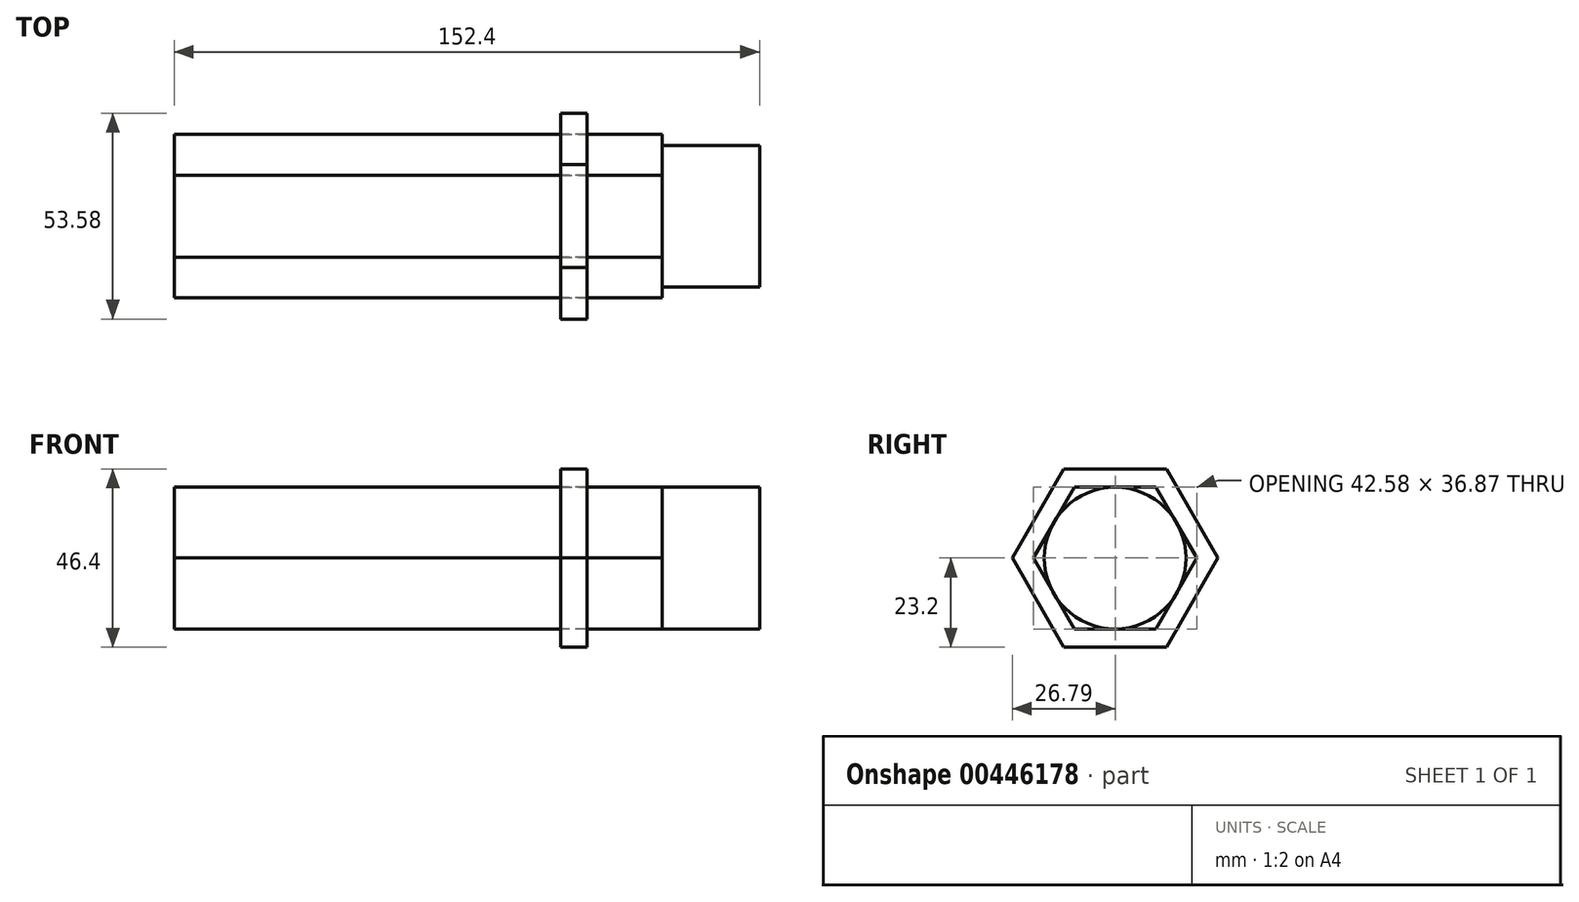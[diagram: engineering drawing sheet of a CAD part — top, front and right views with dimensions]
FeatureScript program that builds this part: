
annotation { "Feature Type Name" : "Feature", "Feature Type Description" : "" }
export const myFeature = defineFeature(function(context is Context, id is Id, definition is map)
    precondition{}
    {
        {
            var Q0;
            Q0=qCreatedBy(makeId("Right.planeOp"),FACE);
            var sketch = newSketch(context, id + "F0", { "sketchPlane" : qUnion([Q0])});
            skCircle(sketch, "E0.cCircle", {"center": v(0, 0) * mm, "radius": 18.44 * mm, "construction": true});
            skLineSegment(sketch, "E0.0", {"start": v(-10.65, 18.44) * mm, "end": v(10.65, 18.44) * mm});
            skLineSegment(sketch, "E0.1", {"start": v(10.65, 18.44) * mm, "end": v(21.3, 0) * mm});
            skLineSegment(sketch, "E0.2", {"start": v(21.3, 0) * mm, "end": v(10.65, -18.44) * mm});
            skLineSegment(sketch, "E0.3", {"start": v(10.65, -18.44) * mm, "end": v(-10.65, -18.44) * mm});
            skLineSegment(sketch, "E0.4", {"start": v(-10.65, -18.44) * mm, "end": v(-21.3, 0) * mm});
            skLineSegment(sketch, "E0.5", {"start": v(-21.3, 0) * mm, "end": v(-10.65, 18.44) * mm});
            skPoint(sketch, "E0.0.midPoint", {"position": v(0, 18.44) * mm});
            skSolve(sketch);
        }
        {
            var Q0;
            Q0=makeQuery(id+"F0.imprint","IMPRINT",FACE,{"disambiguationData":[TD([[makeQuery(id+"F0.imprint","IMPRINT",EDGE,{"derivedFrom":sQuery(id+"F0.wireOp",EDGE,"E0.0")}),-1.0]])]});
            extrude(context, id + "F1", {"entities" : qUnion([Q0]), "endBound" : BoundingType.SYMMETRIC, "depth" : 127 * mm});
        }
        {
            var Q0;
            Q0=makeQuery(id+"F1.opExtrude","SWEPT_BODY",BODY,{"disambiguationData":[OSD([sQuery(id+"F0.wireOp",EDGE,"E0.0"),sQuery(id+"F0.wireOp",EDGE,"E0.1"),sQuery(id+"F0.wireOp",EDGE,"E0.2"),sQuery(id+"F0.wireOp",EDGE,"E0.3"),sQuery(id+"F0.wireOp",EDGE,"E0.4"),sQuery(id+"F0.wireOp",EDGE,"E0.5")])]});
            deleteBodies(context, id + "F2", {"entities" : qUnion([Q0])});
        }
        {
            var Q0;
            Q0=makeQuery(id+"F0.imprint","IMPRINT",FACE,{"disambiguationData":[TD([[makeQuery(id+"F0.imprint","IMPRINT",EDGE,{"derivedFrom":sQuery(id+"F0.wireOp",EDGE,"E0.0")}),-1.0]])]});
            extrude(context, id + "F3", {"entities" : qUnion([Q0]), "endBound" : BoundingType.SYMMETRIC, "depth" : 127 * mm});
        }
        {
            var Q0;
            Q0=makeQuery(id+"F3.opExtrude","CAP_FACE",FACE,{"disambiguationData":[OSD([sQuery(id+"F0.wireOp",EDGE,"E0.0"),sQuery(id+"F0.wireOp",EDGE,"E0.1"),sQuery(id+"F0.wireOp",EDGE,"E0.2"),sQuery(id+"F0.wireOp",EDGE,"E0.3"),sQuery(id+"F0.wireOp",EDGE,"E0.4"),sQuery(id+"F0.wireOp",EDGE,"E0.5")])],"isStart":false});
            var sketch = newSketch(context, id + "F4", { "sketchPlane" : qUnion([Q0])});
            skCircle(sketch, "E1", {"center": v(0, 0) * mm, "radius": 18.44 * mm});
            skSolve(sketch);
        }
        {
            var Q0;
            {var subQ0=sQuery(id+"F4.wireOp",EDGE,"E1");var subQ4=makeQuery(id+"F4.imprint","INTERSECT",VERTEX,{"derivedFrom":[makeQuery(id+"F3.opExtrude","CAP_EDGE",EDGE,{"disambiguationData":[OSD([sQuery(id+"F0.wireOp",EDGE,"E0.0")])],"isStart":false}),subQ0]});Q0=makeQuery(id+"F4.imprint","IMPRINT",FACE,{"disambiguationData":[TD([[makeQuery(id+"F4.imprint","IMPRINT",EDGE,{"disambiguationData":[TD([[subQ4,1.0]])],"derivedFrom":subQ0}),1.0]])]});}
            extrude(context, id + "F5", {"entities" : qUnion([Q0]), "operationType" : NewBodyOperationType.ADD, "depth" : 25.4 * mm});
        }
        {
            var Q0;
            Q0=qCreatedBy(makeId("Right.planeOp"),FACE);
            var sketch = newSketch(context, id + "F6", { "sketchPlane" : qUnion([Q0])});
            skCircle(sketch, "E2.cCircle", {"center": v(0, 0) * mm, "radius": 23.2 * mm, "construction": true});
            skLineSegment(sketch, "E2.0", {"start": v(-13.4, 23.2) * mm, "end": v(13.4, 23.2) * mm});
            skLineSegment(sketch, "E2.1", {"start": v(13.4, 23.2) * mm, "end": v(26.79, 0) * mm});
            skLineSegment(sketch, "E2.2", {"start": v(26.79, 0) * mm, "end": v(13.4, -23.2) * mm});
            skLineSegment(sketch, "E2.3", {"start": v(13.4, -23.2) * mm, "end": v(-13.4, -23.2) * mm});
            skLineSegment(sketch, "E2.4", {"start": v(-13.4, -23.2) * mm, "end": v(-26.79, 0) * mm});
            skLineSegment(sketch, "E2.5", {"start": v(-26.79, 0) * mm, "end": v(-13.4, 23.2) * mm});
            skPoint(sketch, "E2.0.midPoint", {"position": v(0, 23.2) * mm});
            skCircle(sketch, "E3.cCircle", {"center": v(0, 0) * mm, "radius": 18.44 * mm, "construction": true});
            skLineSegment(sketch, "E3.0", {"start": v(-10.64, 18.44) * mm, "end": v(10.64, 18.44) * mm});
            skLineSegment(sketch, "E3.1", {"start": v(10.64, 18.44) * mm, "end": v(21.29, 0) * mm});
            skLineSegment(sketch, "E3.2", {"start": v(21.29, 0) * mm, "end": v(10.64, -18.44) * mm});
            skLineSegment(sketch, "E3.3", {"start": v(10.64, -18.44) * mm, "end": v(-10.64, -18.44) * mm});
            skLineSegment(sketch, "E3.4", {"start": v(-10.64, -18.44) * mm, "end": v(-21.29, 0) * mm});
            skLineSegment(sketch, "E3.5", {"start": v(-21.29, 0) * mm, "end": v(-10.64, 18.44) * mm});
            skPoint(sketch, "E3.0.midPoint", {"position": v(0, 18.44) * mm});
            skSolve(sketch);
        }
        {
            var Q0;
            Q0=makeQuery(id+"F6.imprint","IMPRINT",FACE,{"disambiguationData":[TD([[makeQuery(id+"F6.imprint","IMPRINT",EDGE,{"derivedFrom":sQuery(id+"F6.wireOp",EDGE,"E2.0")}),-1.0]])]});
            extrude(context, id + "F7", {"entities" : qUnion([Q0]), "depth" : 43.94 * mm});
        }
        {
            var Q0;
            Q0 = qSketchRegion(id + "F6", true);
            extrude(context, id + "F8", {"entities" : qUnion([Q0]), "operationType" : NewBodyOperationType.REMOVE, "depth" : 37.08 * mm});
        }
    });
